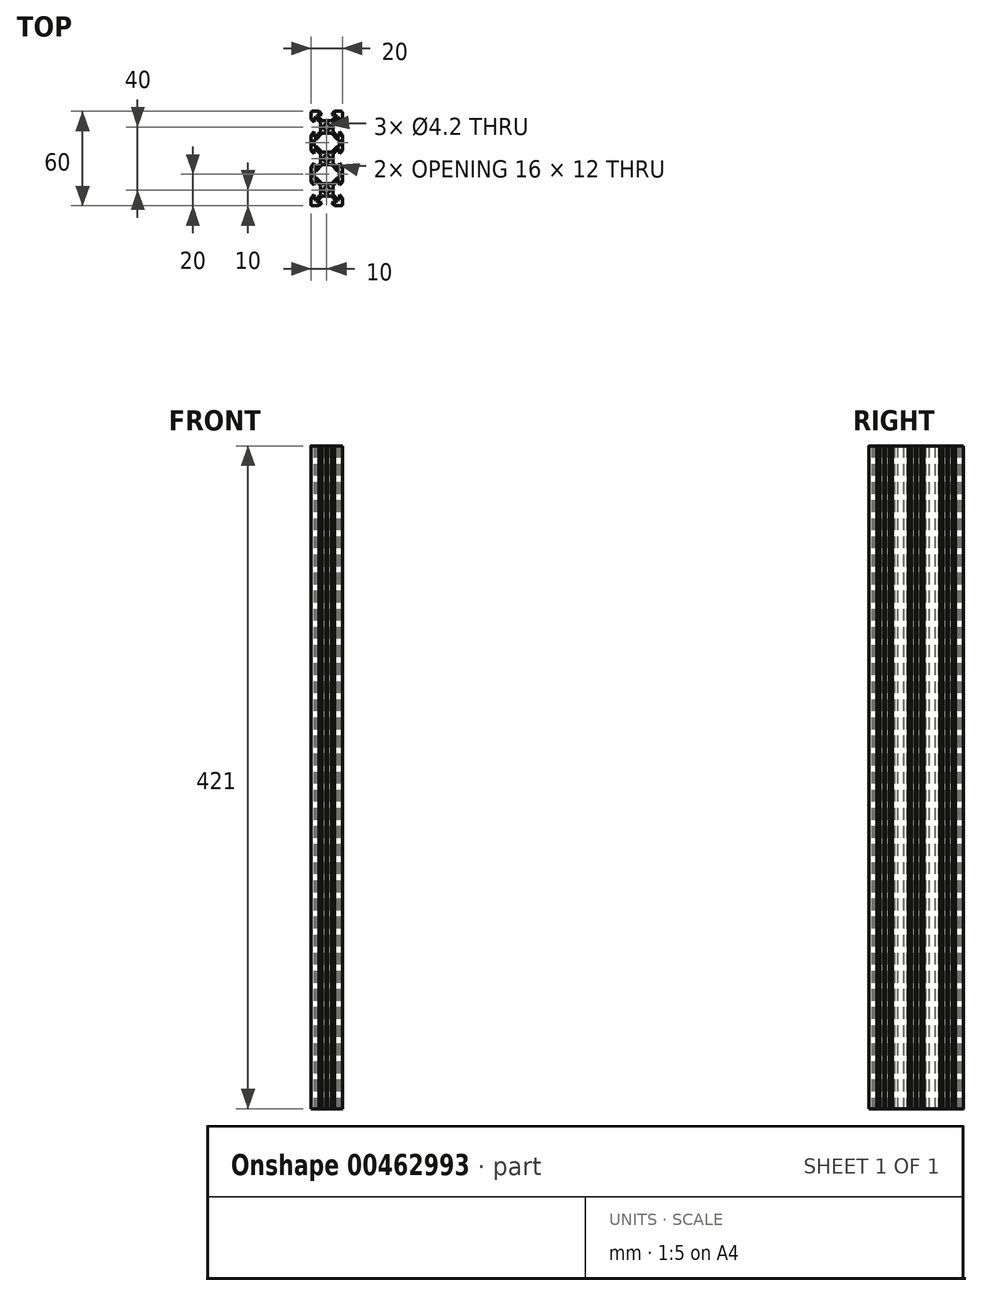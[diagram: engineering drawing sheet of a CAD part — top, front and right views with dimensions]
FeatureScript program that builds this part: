
annotation { "Feature Type Name" : "Feature", "Feature Type Description" : "" }
export const myFeature = defineFeature(function(context is Context, id is Id, definition is map)
    precondition{}
    {
        {
            var Q0;
            Q0=qCreatedBy(makeId("Top.planeOp"),FACE);
            var sketch = newSketch(context, id + "F0", { "sketchPlane" : qUnion([Q0])});
            skLineSegment(sketch, "E0", {"start": v(-10, -5) * mm, "end": v(-10, -15) * mm});
            skLineSegment(sketch, "E1", {"start": v(-8, -17) * mm, "end": v(-8, -14) * mm});
            skLineSegment(sketch, "E2", {"start": v(-8, -14) * mm, "end": v(-7.06, -14) * mm});
            skLineSegment(sketch, "E3", {"start": v(-7.06, -14) * mm, "end": v(-4, -17.06) * mm});
            skLineSegment(sketch, "E4", {"start": v(-4, -17.06) * mm, "end": v(-4, -19.48) * mm});
            skLineSegment(sketch, "E5", {"start": v(-4, -19.48) * mm, "end": v(-3.7, -20) * mm});
            skLineSegment(sketch, "E6", {"start": v(-3.7, -20) * mm, "end": v(-4, -20.52) * mm});
            skLineSegment(sketch, "E7", {"start": v(-4, -20.52) * mm, "end": v(-4, -22.94) * mm});
            skLineSegment(sketch, "E8", {"start": v(-4, -22.94) * mm, "end": v(-7.06, -26) * mm});
            skLineSegment(sketch, "E9", {"start": v(-7.06, -26) * mm, "end": v(-8, -26) * mm});
            skLineSegment(sketch, "E10", {"start": v(-8, -26) * mm, "end": v(-8, -23) * mm});
            skLineSegment(sketch, "E11", {"start": v(-10, -25) * mm, "end": v(-10, -29) * mm});
            skArc(sketch, "E12", {"start": v(-10, -29) * mm, "mid": v(-9.7, -29.7) * mm, "end": v(-9, -30) * mm});
            skLineSegment(sketch, "E13", {"start": v(-9, -30) * mm, "end": v(-5, -30) * mm});
            skLineSegment(sketch, "E14", {"start": v(-3, -28) * mm, "end": v(-6, -28) * mm});
            skLineSegment(sketch, "E15", {"start": v(-6, -28) * mm, "end": v(-6, -27.06) * mm});
            skLineSegment(sketch, "E16", {"start": v(-6, -27.06) * mm, "end": v(-2.94, -24) * mm});
            skLineSegment(sketch, "E17", {"start": v(-2.94, -24) * mm, "end": v(-0.52, -24) * mm});
            skLineSegment(sketch, "E18", {"start": v(-0.52, -24) * mm, "end": v(0, -23.7) * mm});
            skLineSegment(sketch, "E19", {"start": v(0, -23.7) * mm, "end": v(0.52, -24) * mm});
            skLineSegment(sketch, "E20", {"start": v(0.52, -24) * mm, "end": v(2.94, -24) * mm});
            skLineSegment(sketch, "E21", {"start": v(2.94, -24) * mm, "end": v(6, -27.06) * mm});
            skLineSegment(sketch, "E22", {"start": v(6, -27.06) * mm, "end": v(6, -28) * mm});
            skLineSegment(sketch, "E23", {"start": v(6, -28) * mm, "end": v(3, -28) * mm});
            skLineSegment(sketch, "E24", {"start": v(5, -30) * mm, "end": v(9, -30) * mm});
            skArc(sketch, "E25", {"start": v(9, -30) * mm, "mid": v(9.7, -29.7) * mm, "end": v(10, -29) * mm});
            skLineSegment(sketch, "E26", {"start": v(10, -29) * mm, "end": v(10, -25) * mm});
            skLineSegment(sketch, "E27", {"start": v(8, -23) * mm, "end": v(8, -26) * mm});
            skLineSegment(sketch, "E28", {"start": v(8, -26) * mm, "end": v(7.06, -26) * mm});
            skLineSegment(sketch, "E29", {"start": v(7.06, -26) * mm, "end": v(4, -22.94) * mm});
            skLineSegment(sketch, "E30", {"start": v(4, -22.94) * mm, "end": v(4, -20.52) * mm});
            skLineSegment(sketch, "E31", {"start": v(4, -20.52) * mm, "end": v(3.7, -20) * mm});
            skLineSegment(sketch, "E32", {"start": v(3.7, -20) * mm, "end": v(4, -19.48) * mm});
            skLineSegment(sketch, "E33", {"start": v(4, -19.48) * mm, "end": v(4, -17.06) * mm});
            skLineSegment(sketch, "E34", {"start": v(4, -17.06) * mm, "end": v(7.06, -14) * mm});
            skLineSegment(sketch, "E35", {"start": v(7.06, -14) * mm, "end": v(8, -14) * mm});
            skLineSegment(sketch, "E36", {"start": v(8, -14) * mm, "end": v(8, -17) * mm});
            skLineSegment(sketch, "E37", {"start": v(10, -15) * mm, "end": v(10, -5) * mm});
            skLineSegment(sketch, "E38", {"start": v(8, -3) * mm, "end": v(8, -6) * mm});
            skLineSegment(sketch, "E39", {"start": v(8, -6) * mm, "end": v(7.06, -6) * mm});
            skLineSegment(sketch, "E40", {"start": v(7.06, -6) * mm, "end": v(4, -2.94) * mm});
            skLineSegment(sketch, "E41", {"start": v(4, -2.94) * mm, "end": v(4, -0.52) * mm});
            skLineSegment(sketch, "E42", {"start": v(4, -0.52) * mm, "end": v(3.7, 0) * mm});
            skLineSegment(sketch, "E43", {"start": v(3.7, 0) * mm, "end": v(4, 0.52) * mm});
            skLineSegment(sketch, "E44", {"start": v(4, 0.52) * mm, "end": v(4, 2.94) * mm});
            skLineSegment(sketch, "E45", {"start": v(4, 2.94) * mm, "end": v(7.06, 6) * mm});
            skLineSegment(sketch, "E46", {"start": v(7.06, 6) * mm, "end": v(8, 6) * mm});
            skLineSegment(sketch, "E47", {"start": v(8, 6) * mm, "end": v(8, 3) * mm});
            skLineSegment(sketch, "E48", {"start": v(10, 5) * mm, "end": v(10, 15) * mm});
            skLineSegment(sketch, "E49", {"start": v(8, 17) * mm, "end": v(8, 14) * mm});
            skLineSegment(sketch, "E50", {"start": v(8, 14) * mm, "end": v(7.06, 14) * mm});
            skLineSegment(sketch, "E51", {"start": v(7.06, 14) * mm, "end": v(4, 17.06) * mm});
            skLineSegment(sketch, "E52", {"start": v(4, 17.06) * mm, "end": v(4, 19.48) * mm});
            skLineSegment(sketch, "E53", {"start": v(4, 19.48) * mm, "end": v(3.7, 20) * mm});
            skLineSegment(sketch, "E54", {"start": v(3.7, 20) * mm, "end": v(4, 20.52) * mm});
            skLineSegment(sketch, "E55", {"start": v(4, 20.52) * mm, "end": v(4, 22.94) * mm});
            skLineSegment(sketch, "E56", {"start": v(4, 22.94) * mm, "end": v(7.06, 26) * mm});
            skLineSegment(sketch, "E57", {"start": v(7.06, 26) * mm, "end": v(8, 26) * mm});
            skLineSegment(sketch, "E58", {"start": v(8, 26) * mm, "end": v(8, 23) * mm});
            skLineSegment(sketch, "E59", {"start": v(10, 25) * mm, "end": v(10, 29) * mm});
            skArc(sketch, "E60", {"start": v(10, 29) * mm, "mid": v(9.7, 29.7) * mm, "end": v(9, 30) * mm});
            skLineSegment(sketch, "E61", {"start": v(9, 30) * mm, "end": v(5, 30) * mm});
            skLineSegment(sketch, "E62", {"start": v(3, 28) * mm, "end": v(6, 28) * mm});
            skLineSegment(sketch, "E63", {"start": v(6, 28) * mm, "end": v(6, 27.06) * mm});
            skLineSegment(sketch, "E64", {"start": v(6, 27.06) * mm, "end": v(2.94, 24) * mm});
            skLineSegment(sketch, "E65", {"start": v(2.94, 24) * mm, "end": v(0.52, 24) * mm});
            skLineSegment(sketch, "E66", {"start": v(0.52, 24) * mm, "end": v(0, 23.7) * mm});
            skLineSegment(sketch, "E67", {"start": v(0, 23.7) * mm, "end": v(-0.52, 24) * mm});
            skLineSegment(sketch, "E68", {"start": v(-0.52, 24) * mm, "end": v(-2.94, 24) * mm});
            skLineSegment(sketch, "E69", {"start": v(-2.94, 24) * mm, "end": v(-6, 27.06) * mm});
            skLineSegment(sketch, "E70", {"start": v(-6, 27.06) * mm, "end": v(-6, 28) * mm});
            skLineSegment(sketch, "E71", {"start": v(-6, 28) * mm, "end": v(-3, 28) * mm});
            skLineSegment(sketch, "E72", {"start": v(-5, 30) * mm, "end": v(-9, 30) * mm});
            skArc(sketch, "E73", {"start": v(-9, 30) * mm, "mid": v(-9.7, 29.7) * mm, "end": v(-10, 29) * mm});
            skLineSegment(sketch, "E74", {"start": v(-10, 29) * mm, "end": v(-10, 25) * mm});
            skLineSegment(sketch, "E75", {"start": v(-8, 23) * mm, "end": v(-8, 26) * mm});
            skLineSegment(sketch, "E76", {"start": v(-8, 26) * mm, "end": v(-7.06, 26) * mm});
            skLineSegment(sketch, "E77", {"start": v(-7.06, 26) * mm, "end": v(-4, 22.94) * mm});
            skLineSegment(sketch, "E78", {"start": v(-4, 22.94) * mm, "end": v(-4, 20.52) * mm});
            skLineSegment(sketch, "E79", {"start": v(-4, 20.52) * mm, "end": v(-3.7, 20) * mm});
            skLineSegment(sketch, "E80", {"start": v(-3.7, 20) * mm, "end": v(-4, 19.48) * mm});
            skLineSegment(sketch, "E81", {"start": v(-4, 19.48) * mm, "end": v(-4, 17.06) * mm});
            skLineSegment(sketch, "E82", {"start": v(-4, 17.06) * mm, "end": v(-7.06, 14) * mm});
            skLineSegment(sketch, "E83", {"start": v(-7.06, 14) * mm, "end": v(-8, 14) * mm});
            skLineSegment(sketch, "E84", {"start": v(-8, 14) * mm, "end": v(-8, 17) * mm});
            skLineSegment(sketch, "E85", {"start": v(-10, 15) * mm, "end": v(-10, 5) * mm});
            skLineSegment(sketch, "E86", {"start": v(-8, 3) * mm, "end": v(-8, 6) * mm});
            skLineSegment(sketch, "E87", {"start": v(-8, 6) * mm, "end": v(-7.06, 6) * mm});
            skLineSegment(sketch, "E88", {"start": v(-7.06, 6) * mm, "end": v(-4, 2.94) * mm});
            skLineSegment(sketch, "E89", {"start": v(-4, 2.94) * mm, "end": v(-4, 0.52) * mm});
            skLineSegment(sketch, "E90", {"start": v(-4, 0.52) * mm, "end": v(-3.7, 0) * mm});
            skLineSegment(sketch, "E91", {"start": v(-3.7, 0) * mm, "end": v(-4, -0.52) * mm});
            skLineSegment(sketch, "E92", {"start": v(-4, -0.52) * mm, "end": v(-4, -2.94) * mm});
            skLineSegment(sketch, "E93", {"start": v(-4, -2.94) * mm, "end": v(-7.06, -6) * mm});
            skLineSegment(sketch, "E94", {"start": v(-7.06, -6) * mm, "end": v(-8, -6) * mm});
            skLineSegment(sketch, "E95", {"start": v(-8, -6) * mm, "end": v(-8, -3) * mm});
            skLineSegment(sketch, "E96", {"start": v(-8, 12) * mm, "end": v(-8, 8) * mm});
            skLineSegment(sketch, "E97", {"start": v(-6.94, 12) * mm, "end": v(-8, 12) * mm});
            skLineSegment(sketch, "E98", {"start": v(-2.94, 16) * mm, "end": v(-6.94, 12) * mm});
            skLineSegment(sketch, "E99", {"start": v(2.94, 16) * mm, "end": v(-2.94, 16) * mm});
            skLineSegment(sketch, "E100", {"start": v(6.94, 12) * mm, "end": v(2.94, 16) * mm});
            skLineSegment(sketch, "E101", {"start": v(8, 12) * mm, "end": v(6.94, 12) * mm});
            skLineSegment(sketch, "E102", {"start": v(8, 8) * mm, "end": v(8, 12) * mm});
            skLineSegment(sketch, "E103", {"start": v(6.94, 8) * mm, "end": v(8, 8) * mm});
            skLineSegment(sketch, "E104", {"start": v(2.94, 4) * mm, "end": v(6.94, 8) * mm});
            skLineSegment(sketch, "E105", {"start": v(-2.94, 4) * mm, "end": v(2.94, 4) * mm});
            skLineSegment(sketch, "E106", {"start": v(-6.94, 8) * mm, "end": v(-2.94, 4) * mm});
            skLineSegment(sketch, "E107", {"start": v(-6.94, -8) * mm, "end": v(-8, -8) * mm});
            skLineSegment(sketch, "E108", {"start": v(-2.94, -4) * mm, "end": v(-6.94, -8) * mm});
            skLineSegment(sketch, "E109", {"start": v(2.94, -4) * mm, "end": v(-2.94, -4) * mm});
            skLineSegment(sketch, "E110", {"start": v(6.94, -8) * mm, "end": v(2.94, -4) * mm});
            skLineSegment(sketch, "E111", {"start": v(8, -8) * mm, "end": v(6.94, -8) * mm});
            skLineSegment(sketch, "E112", {"start": v(8, -12) * mm, "end": v(8, -8) * mm});
            skLineSegment(sketch, "E113", {"start": v(6.94, -12) * mm, "end": v(8, -12) * mm});
            skLineSegment(sketch, "E114", {"start": v(2.94, -16) * mm, "end": v(6.94, -12) * mm});
            skLineSegment(sketch, "E115", {"start": v(-2.94, -16) * mm, "end": v(2.94, -16) * mm});
            skLineSegment(sketch, "E116", {"start": v(-6.94, -12) * mm, "end": v(-2.94, -16) * mm});
            skLineSegment(sketch, "E117", {"start": v(-8, -12) * mm, "end": v(-6.94, -12) * mm});
            skLineSegment(sketch, "E118", {"start": v(-8, 8) * mm, "end": v(-6.94, 8) * mm});
            skLineSegment(sketch, "E119", {"start": v(-8, -8) * mm, "end": v(-8, -12) * mm});
            skCircle(sketch, "E120", {"center": v(0, -20) * mm, "radius": 2.1 * mm});
            skCircle(sketch, "E121", {"center": v(0, 0) * mm, "radius": 2.1 * mm});
            skCircle(sketch, "E122", {"center": v(0, 20) * mm, "radius": 2.1 * mm});
            skLineSegment(sketch, "E123", {"start": v(-8, 17) * mm, "end": v(-10, 15) * mm});
            skLineSegment(sketch, "E124", {"start": v(-8, 3) * mm, "end": v(-10, 5) * mm});
            skLineSegment(sketch, "E125", {"start": v(8, 17) * mm, "end": v(10, 15) * mm});
            skLineSegment(sketch, "E126", {"start": v(8, 3) * mm, "end": v(10, 5) * mm});
            skLineSegment(sketch, "E127", {"start": v(8, 23) * mm, "end": v(10, 25) * mm});
            skLineSegment(sketch, "E128", {"start": v(3, 28) * mm, "end": v(5, 30) * mm});
            skLineSegment(sketch, "E129", {"start": v(-3, 28) * mm, "end": v(-5, 30) * mm});
            skLineSegment(sketch, "E130", {"start": v(-8, 23) * mm, "end": v(-10, 25) * mm});
            skLineSegment(sketch, "E131", {"start": v(-8, -3) * mm, "end": v(-10, -5) * mm});
            skLineSegment(sketch, "E132", {"start": v(-8, -17) * mm, "end": v(-10, -15) * mm});
            skLineSegment(sketch, "E133", {"start": v(-8, -23) * mm, "end": v(-10, -25) * mm});
            skLineSegment(sketch, "E134", {"start": v(-3, -28) * mm, "end": v(-5, -30) * mm});
            skLineSegment(sketch, "E135", {"start": v(3, -28) * mm, "end": v(5, -30) * mm});
            skLineSegment(sketch, "E136", {"start": v(8, -23) * mm, "end": v(10, -25) * mm});
            skLineSegment(sketch, "E137", {"start": v(8, -17) * mm, "end": v(10, -15) * mm});
            skLineSegment(sketch, "E138", {"start": v(8, -3) * mm, "end": v(10, -5) * mm});
            skSolve(sketch);
        }
        {
            var Q0;
            Q0=qSketchRegion(id+"F0",true);
            extrude(context, id + "F1", {"entities" : qUnion([Q0]), "depth" : 421 * mm, "offsetDistance" : 25 * mm});
        }
    });
